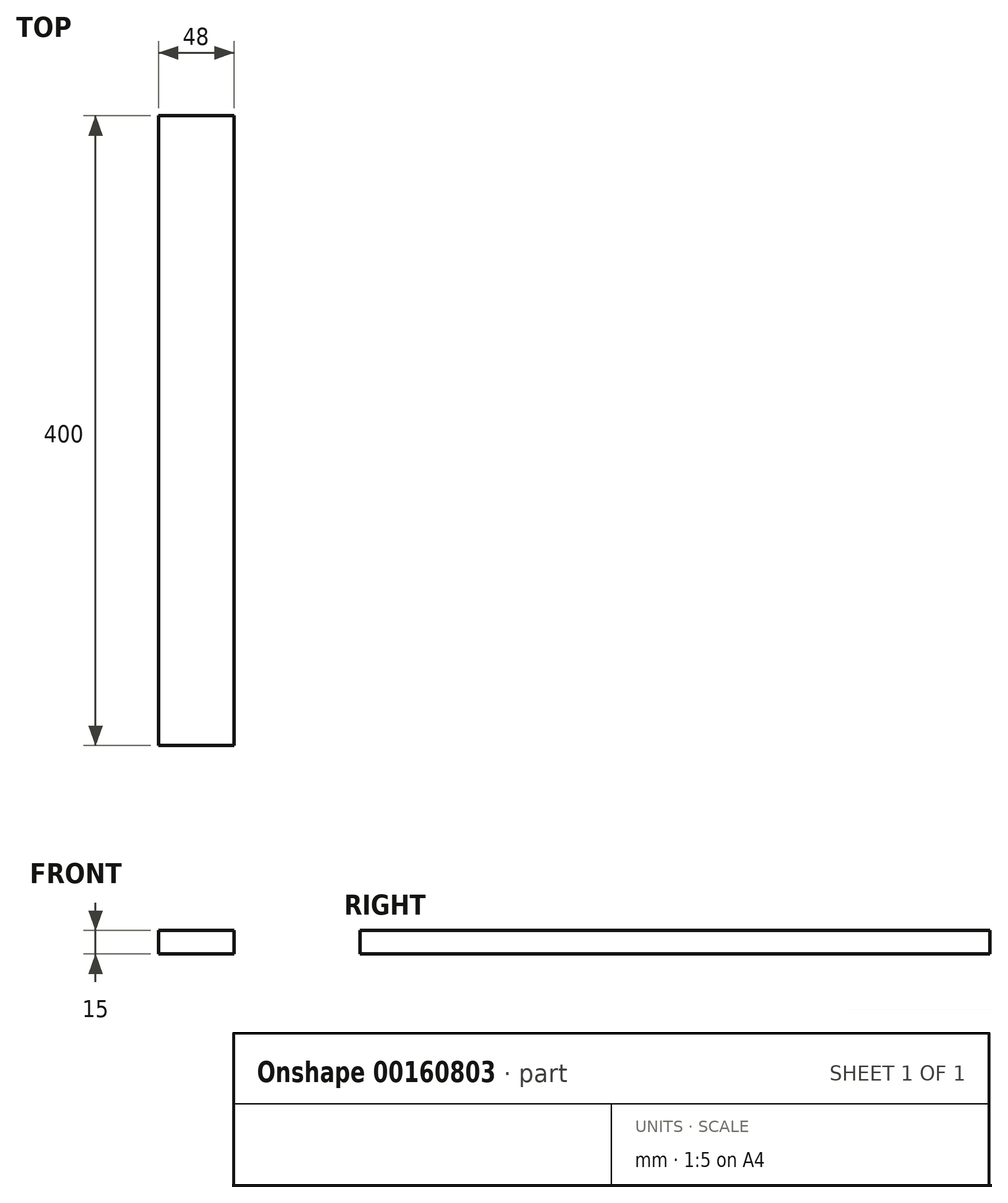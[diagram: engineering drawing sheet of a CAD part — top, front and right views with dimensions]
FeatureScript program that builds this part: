
annotation { "Feature Type Name" : "Feature", "Feature Type Description" : "" }
export const myFeature = defineFeature(function(context is Context, id is Id, definition is map)
    precondition{}
    {
        {
            var Q0;
            Q0=qCreatedBy(makeId("Front.planeOp"),FACE);
            var sketch = newSketch(context, id + "F0", { "sketchPlane" : qUnion([Q0])});
            skLineSegment(sketch, "E0.bottom", {"start": v(-74.1, 26.2) * mm, "end": v(-26.1, 26.2) * mm});
            skLineSegment(sketch, "E0.top", {"start": v(-74.1, 11.2) * mm, "end": v(-26.1, 11.2) * mm});
            skLineSegment(sketch, "E0.left", {"start": v(-74.1, 26.2) * mm, "end": v(-74.1, 11.2) * mm});
            skLineSegment(sketch, "E0.right", {"start": v(-26.1, 26.2) * mm, "end": v(-26.1, 11.2) * mm});
            skSolve(sketch);
        }
        {
            var Q0;
            Q0=makeQuery(id+"F0.imprint","IMPRINT",FACE,{"disambiguationData":[TD([[makeQuery(id+"F0.imprint","IMPRINT",EDGE,{"derivedFrom":sQuery(id+"F0.wireOp",EDGE,"E0.bottom")}),-1.0]])]});
            extrude(context, id + "F1", {"entities" : qUnion([Q0]), "depth" : 400 * mm});
        }
    });
